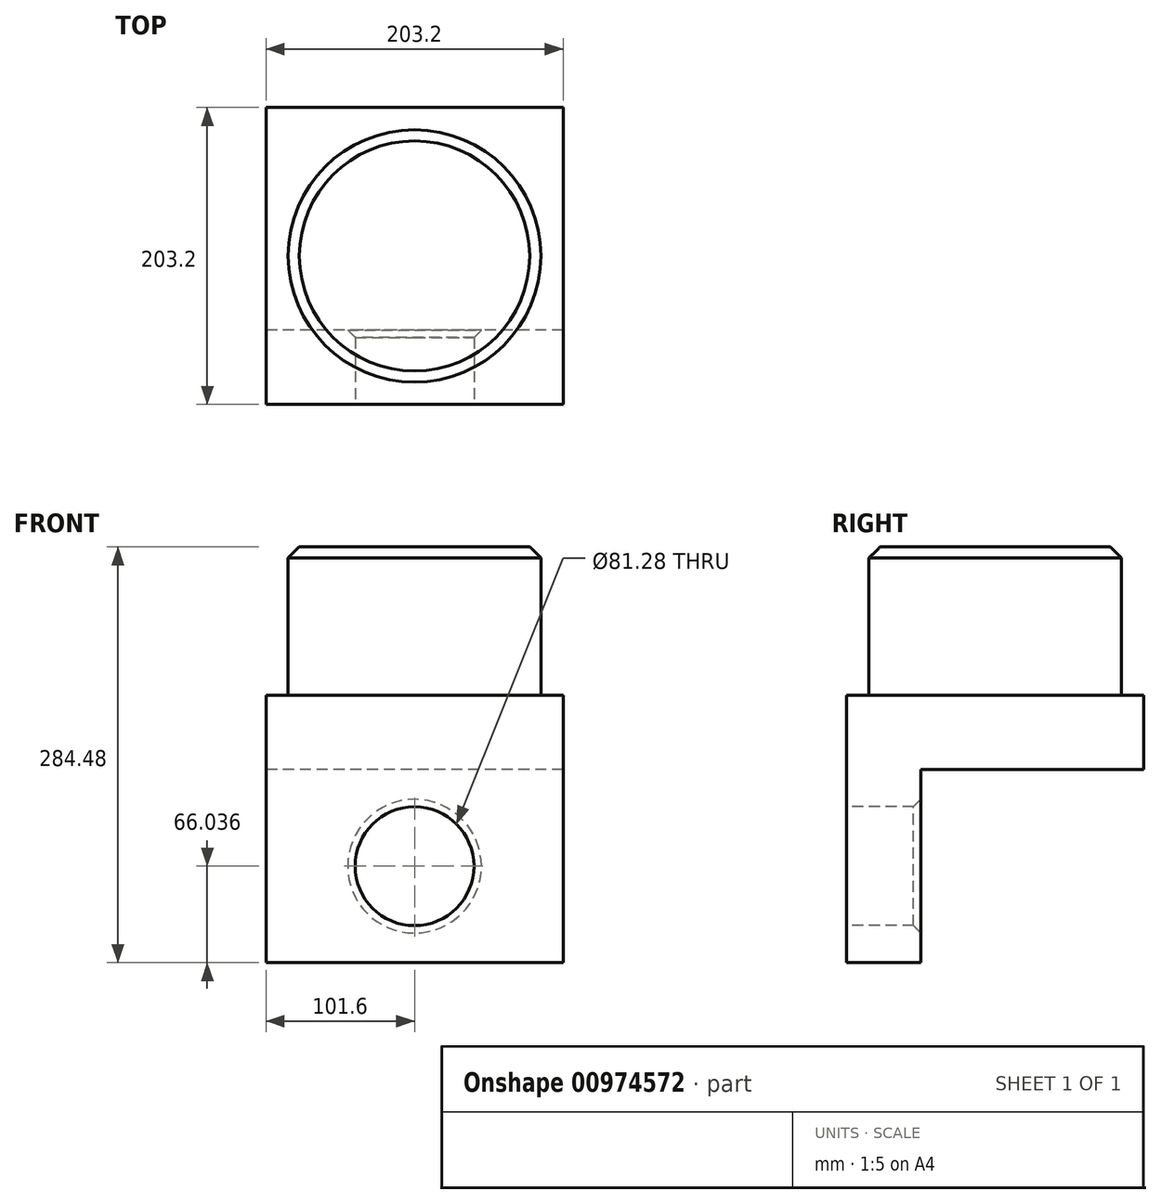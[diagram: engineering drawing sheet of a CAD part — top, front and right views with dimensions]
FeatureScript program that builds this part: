
annotation { "Feature Type Name" : "Feature", "Feature Type Description" : "" }
export const myFeature = defineFeature(function(context is Context, id is Id, definition is map)
    precondition{}
    {
        {
            var Q0;
            Q0=qCreatedBy(makeId("Right.planeOp"),FACE);
            var sketch = newSketch(context, id + "F0", { "sketchPlane" : qUnion([Q0])});
            skLineSegment(sketch, "E0", {"start": v(-50.6, -72.23) * mm, "end": v(-50.6, 59.85) * mm});
            skLineSegment(sketch, "E1", {"start": v(-50.6, 59.85) * mm, "end": v(101.8, 59.85) * mm});
            skLineSegment(sketch, "E2", {"start": v(101.8, 59.85) * mm, "end": v(101.8, 110.65) * mm});
            skLineSegment(sketch, "E3", {"start": v(101.8, 110.65) * mm, "end": v(-101.4, 110.65) * mm});
            skLineSegment(sketch, "E4", {"start": v(-101.4, 110.65) * mm, "end": v(-101.4, -72.23) * mm});
            skLineSegment(sketch, "E5", {"start": v(-101.4, -72.23) * mm, "end": v(-50.6, -72.23) * mm});
            skSolve(sketch);
        }
        {
            var Q0;
            Q0=makeQuery(id+"F0.imprint","IMPRINT",FACE,{"disambiguationData":[TD([[makeQuery(id+"F0.imprint","IMPRINT",EDGE,{"derivedFrom":sQuery(id+"F0.wireOp",EDGE,"E0")}),1.0]])]});
            extrude(context, id + "F1", {"entities" : qUnion([Q0]), "depth" : 203.2 * mm, "offsetDistance" : 25.4 * mm});
        }
        {
            var Q0;
            Q0=makeQuery(id+"F1.opExtrude","SWEPT_FACE",FACE,{"disambiguationData":[OSD([sQuery(id+"F0.wireOp",EDGE,"E4")])]});
            var sketch = newSketch(context, id + "F2", { "sketchPlane" : qUnion([Q0])});
            skCircle(sketch, "E6", {"center": v(101.6, -6.2) * mm, "radius": 40.64 * mm});
            skSolve(sketch);
        }
        {
            var Q0;
            Q0=makeQuery(id+"F2.imprint","IMPRINT",FACE,{"disambiguationData":[TD([[makeQuery(id+"F2.imprint","IMPRINT",EDGE,{"derivedFrom":sQuery(id+"F2.wireOp",EDGE,"E6")}),1.0]])]});
            extrude(context, id + "F3", {"entities" : qUnion([Q0]), "operationType" : NewBodyOperationType.REMOVE, "oppositeDirection" : true, "depth" : 635 * mm, "offsetDistance" : 25.4 * mm});
        }
        {
            var Q0;
            Q0=makeQuery(id+"F1.opExtrude","SWEPT_FACE",FACE,{"disambiguationData":[OSD([sQuery(id+"F0.wireOp",EDGE,"E3")])]});
            var sketch = newSketch(context, id + "F4", { "sketchPlane" : qUnion([Q0])});
            skCircle(sketch, "E7", {"center": v(101.6, 0.2) * mm, "radius": 86.36 * mm});
            skSolve(sketch);
        }
        {
            var Q0;
            Q0=makeQuery(id+"F4.imprint","IMPRINT",FACE,{"disambiguationData":[TD([[makeQuery(id+"F4.imprint","IMPRINT",EDGE,{"derivedFrom":sQuery(id+"F4.wireOp",EDGE,"E7")}),1.0]])]});
            extrude(context, id + "F5", {"entities" : qUnion([Q0]), "operationType" : NewBodyOperationType.ADD, "depth" : 101.6 * mm, "offsetDistance" : 25.4 * mm});
        }
        {
            var Q0;
            Q0=makeQuery(id+"F5.opExtrude","CAP_EDGE",EDGE,{"disambiguationData":[OSD([sQuery(id+"F4.wireOp",EDGE,"E7")])],"isStart":false});
            chamfer(context, id + "F6", {"entities" : qUnion([Q0]), "chamferType" : ChamferType.OFFSET_ANGLE, "width" : 7.62 * mm, "oppositeDirection" : false, "angle" : 45 * degree, "tangentPropagation" : true});
        }
        {
            var Q0;
            Q0=makeQuery(id+"F3.boolean.opBoolean","COPY",EDGE,{"derivedFrom":makeQuery(id+"F3.opExtrude","CAP_EDGE",EDGE,{"disambiguationData":[OSD([sQuery(id+"F2.wireOp",EDGE,"E6")])],"isStart":true})});
            var Q1;
            Q1=makeQuery(id+"F3.boolean.opBoolean","INTERSECT",EDGE,{"derivedFrom":[makeQuery(id+"F1.opExtrude","SWEPT_FACE",FACE,{"disambiguationData":[OSD([sQuery(id+"F0.wireOp",EDGE,"E0")])]}),makeQuery(id+"F3.opExtrude","SWEPT_FACE",FACE,{"disambiguationData":[OSD([sQuery(id+"F2.wireOp",EDGE,"E6")])]})]});
            chamfer(context, id + "F7", {"entities" : qUnion([Q0, Q1]), "chamferType" : ChamferType.OFFSET_ANGLE, "width" : 5.08 * mm, "oppositeDirection" : false, "angle" : 45 * degree, "tangentPropagation" : true});
        }
    });
